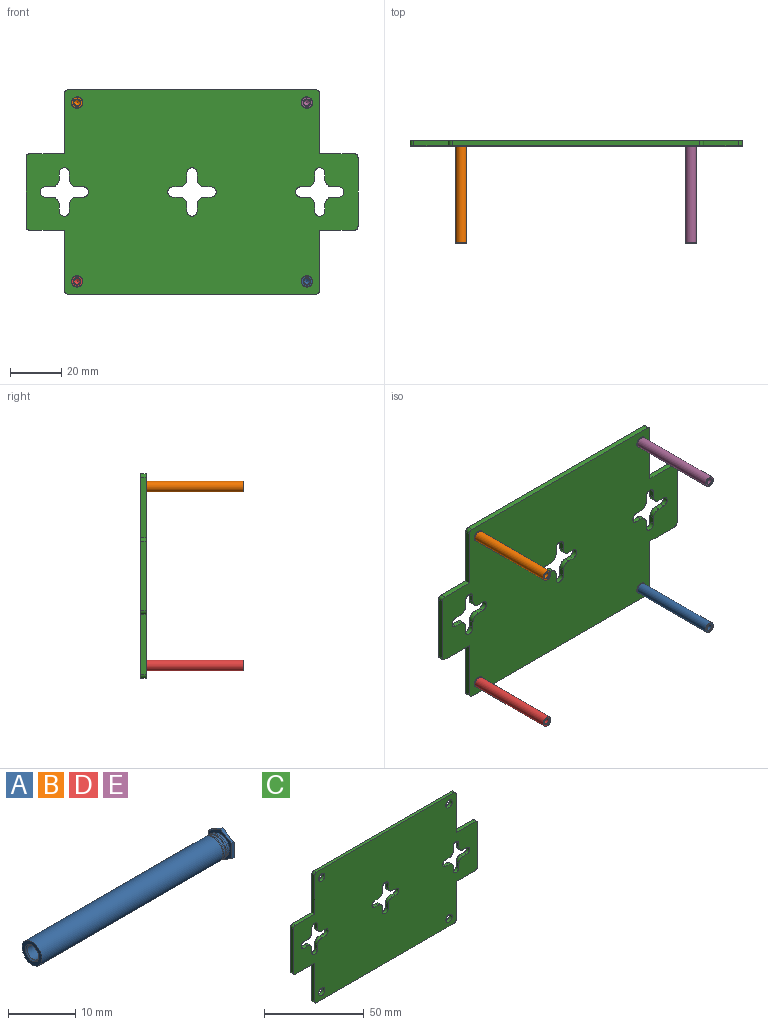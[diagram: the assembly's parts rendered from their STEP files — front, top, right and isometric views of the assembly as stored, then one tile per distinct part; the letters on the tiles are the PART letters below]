
ASSEMBLY  parts=5 mates=1
PART A: 25 faces, bbox 40x4.8x5.5 mm
  f0: plane 5.54x4.8mm, normal (1,0,0), area 20mm2, adj f1,f2,f3,f4,f5,f6
  f1: plane 2.4x1.39mm, normal (0,-0.5,0.87), area 1.3mm2, adj f0,f2,f6,f7
  f2: plane 2.77x0.48mm, normal (0,-1,0), area 1.3mm2, adj f0,f1,f3,f7
  f3: plane 2.4x1.39mm, normal (0,-0.5,-0.87), area 1.3mm2, adj f0,f2,f4,f7
  f4: plane 2.4x1.39mm, normal (0,0.5,-0.87), area 1.3mm2, adj f0,f3,f5,f7
  f5: plane 2.77x0.48mm, normal (0,1,0), area 1.3mm2, adj f0,f4,f6,f7
  f6: plane 2.4x1.39mm, normal (0,0.5,0.87), area 1.3mm2, adj f0,f1,f5,f7
  f7: plane 5.54x4.8mm, normal (-1,0,0), area 8.7mm2, adj f1,f2,f3,f4,f5,f6,f8
  f8: cylinder r=1.89mm len=3.78mm, axis (1,0,0), area 5.7mm2, adj f7,f9
  f9: plane 4.2x4.2mm, normal (1,0,0), area 2.6mm2, adj f8,f10
  f10: cylinder r=2.1mm len=4.2mm, axis (1,0,0), area 4.4mm2, adj f9,f11
  f11: plane 4.2x4.2mm, normal (-1,0,0), area 1.4mm2, adj f10,f12
  f12: cylinder r=1.99mm len=3.99mm, axis (1,0,0), area 2.6mm2, adj f11,f14
  f13: cone r=0.61mm half-angle=60deg, axis (-1,0,0), area 5.5mm2, adj f15
  f14: plane 4.2x4.2mm, normal (1,0,0), area 1.4mm2, adj f12,f16
  f15: cylinder r=1.23mm len=7.75mm, axis (-1,0,0), area 59.9mm2, adj f13,f17
  f16: cylinder r=2.1mm len=4.2mm, axis (1,0,0), area 4.4mm2, adj f14,f18
  f17: plane 2.46x2.46mm, normal (1,0,0), area 0mm2, adj f15,f19
  f18: plane 4.2x4.2mm, normal (-1,0,0), area 1.4mm2, adj f16,f20
  f19: cylinder r=1.22mm len=24.3mm, axis (-1,0,0), area 187mm2, adj f17,f24
  f20: cylinder r=1.99mm len=3.99mm, axis (1,0,0), area 2.6mm2, adj f18,f21
  f21: plane 4.2x4.2mm, normal (1,0,0), area 1.4mm2, adj f20,f23
  f22: plane 4.2x4.2mm, normal (-1,0,0), area 7.5mm2, adj f23,f24
  f23: cylinder r=2.1mm len=37.95mm, axis (1,0,0), area 500.7mm2, adj f21,f22
  f24: cone r=1.22mm half-angle=45deg, axis (-1,0,0), area 2.4mm2, adj f19,f22
PART B: same geometry as A
PART C: 74 faces, bbox 130x2x80 mm
  f0: plane 23.5x2mm, normal (-1,0,0), area 47mm2, adj f6,f7,f11,f73
  f1: plane 23.5x2mm, normal (1,0,0), area 47mm2, adj f6,f7,f10,f70
  f2: plane 23.5x2mm, normal (-1,0,0), area 47mm2, adj f6,f7,f12,f71
  f3: plane 97x2mm, normal (0,0,-1), area 194mm2, adj f6,f7,f71,f72
  f4: plane 23.5x2mm, normal (1,0,0), area 47mm2, adj f6,f7,f9,f72
  f5: plane 97x2mm, normal (0,0,1), area 194mm2, adj f6,f7,f70,f73
  f6: plane 130x80mm, normal (0,-1,0), area 8421.9mm2, adj f0,f1,f2,f3,f4,f5,f8,f9
  f7: plane 130x80mm, normal (0,1,0), area 8421.9mm2, adj f0,f1,f2,f3,f4,f5,f8,f9
  f8: plane 27x2mm, normal (1,0,0), area 54mm2, adj f6,f7,f68,f69
  f9: plane 13.5x2mm, normal (0,0,-1), area 27mm2, adj f4,f6,f7,f68
  f10: plane 13.5x2mm, normal (0,0,1), area 27mm2, adj f1,f6,f7,f69
  f11: plane 13.5x2mm, normal (0,0,1), area 27mm2, adj f0,f6,f7,f66
  f12: plane 13.5x2mm, normal (0,0,-1), area 27mm2, adj f2,f6,f7,f67
  f13: plane 27x2mm, normal (-1,0,0), area 54mm2, adj f6,f7,f66,f67
  f14: cylinder r=2.25mm len=4.5mm, axis (0,-1,0), area 28.3mm2, adj f6,f7
  f15: plane 2.5x2mm, normal (1,0,0), area 5mm2, adj f6,f7,f26,f56
  f16: plane 2.5x2mm, normal (0,0,-1), area 5mm2, adj f6,f7,f17,f56
  f17: cylinder r=2mm len=4mm, axis (0,-1,0), area 12.6mm2, adj f6,f7,f16,f18
  f18: plane 2.5x2mm, normal (0,0,1), area 5mm2, adj f6,f7,f17,f55
  f19: plane 2.5x2mm, normal (1,0,0), area 5mm2, adj f6,f7,f20,f55
  f20: cylinder r=2mm len=4mm, axis (0,-1,0), area 12.6mm2, adj f6,f7,f19,f21
  f21: plane 2.5x2mm, normal (-1,0,0), area 5mm2, adj f6,f7,f20,f54
  f22: plane 2.5x2mm, normal (0,0,1), area 5mm2, adj f6,f7,f23,f54
  f23: cylinder r=2mm len=4mm, axis (0,-1,0), area 12.6mm2, adj f6,f7,f22,f24
  f24: plane 2.5x2mm, normal (0,0,-1), area 5mm2, adj f6,f7,f23,f57
  f25: plane 2.5x2mm, normal (-1,0,0), area 5mm2, adj f6,f7,f26,f57
  f26: cylinder r=2mm len=4mm, axis (0,-1,0), area 12.6mm2, adj f6,f7,f15,f25
  f27: plane 2.5x2mm, normal (1,0,0), area 5mm2, adj f6,f7,f38,f60
  f28: plane 2.5x2mm, normal (0,0,-1), area 5mm2, adj f6,f7,f29,f60
  f29: cylinder r=2mm len=4mm, axis (0,-1,0), area 12.6mm2, adj f6,f7,f28,f30
  f30: plane 2.5x2mm, normal (0,0,1), area 5mm2, adj f6,f7,f29,f59
  f31: plane 2.5x2mm, normal (1,0,0), area 5mm2, adj f6,f7,f32,f59
  f32: cylinder r=2mm len=4mm, axis (0,-1,0), area 12.6mm2, adj f6,f7,f31,f33
  f33: plane 2.5x2mm, normal (-1,0,0), area 5mm2, adj f6,f7,f32,f58
  f34: plane 2.5x2mm, normal (0,0,1), area 5mm2, adj f6,f7,f35,f58
  f35: cylinder r=2mm len=4mm, axis (0,-1,0), area 12.6mm2, adj f6,f7,f34,f36
  f36: plane 2.5x2mm, normal (0,0,-1), area 5mm2, adj f6,f7,f35,f61
  f37: plane 2.5x2mm, normal (-1,0,0), area 5mm2, adj f6,f7,f38,f61
  f38: cylinder r=2mm len=4mm, axis (0,-1,0), area 12.6mm2, adj f6,f7,f27,f37
  f39: cylinder r=2.25mm len=4.5mm, axis (0,-1,0), area 28.3mm2, adj f6,f7
  f40: cylinder r=2.25mm len=4.5mm, axis (0,-1,0), area 28.3mm2, adj f6,f7
  f41: cylinder r=2.25mm len=4.5mm, axis (0,-1,0), area 28.3mm2, adj f6,f7
  f42: plane 2.5x2mm, normal (1,0,0), area 5mm2, adj f6,f7,f53,f64
  f43: plane 2.5x2mm, normal (0,0,-1), area 5mm2, adj f6,f7,f44,f64
  f44: cylinder r=2mm len=4mm, axis (0,-1,0), area 12.6mm2, adj f6,f7,f43,f45
  f45: plane 2.5x2mm, normal (0,0,1), area 5mm2, adj f6,f7,f44,f62
  f46: plane 2.5x2mm, normal (1,0,0), area 5mm2, adj f6,f7,f47,f62
  f47: cylinder r=2mm len=4mm, axis (0,-1,0), area 12.6mm2, adj f6,f7,f46,f48
  f48: plane 2.5x2mm, normal (-1,0,0), area 5mm2, adj f6,f7,f47,f63
  f49: plane 2.5x2mm, normal (0,0,1), area 5mm2, adj f6,f7,f50,f63
  f50: cylinder r=2mm len=4mm, axis (0,-1,0), area 12.6mm2, adj f6,f7,f49,f51
  f51: plane 2.5x2mm, normal (0,0,-1), area 5mm2, adj f6,f7,f50,f65
  f52: plane 2.5x2mm, normal (-1,0,0), area 5mm2, adj f6,f7,f53,f65
  f53: cylinder r=2mm len=4mm, axis (0,-1,0), area 12.6mm2, adj f6,f7,f42,f52
  f54: cylinder r=3mm len=3mm, axis (0,1,0), area 9.4mm2, adj f6,f7,f21,f22
  f55: cylinder r=3mm len=3mm, axis (0,-1,0), area 9.4mm2, adj f6,f7,f18,f19
  f56: cylinder r=3mm len=3mm, axis (0,1,0), area 9.4mm2, adj f6,f7,f15,f16
  f57: cylinder r=3mm len=3mm, axis (0,-1,0), area 9.4mm2, adj f6,f7,f24,f25
  f58: cylinder r=3mm len=3mm, axis (0,1,0), area 9.4mm2, adj f6,f7,f33,f34
  f59: cylinder r=3mm len=3mm, axis (0,-1,0), area 9.4mm2, adj f6,f7,f30,f31
  f60: cylinder r=3mm len=3mm, axis (0,1,0), area 9.4mm2, adj f6,f7,f27,f28
  f61: cylinder r=3mm len=3mm, axis (0,-1,0), area 9.4mm2, adj f6,f7,f36,f37
  f62: cylinder r=3mm len=3mm, axis (0,-1,0), area 9.4mm2, adj f6,f7,f45,f46
  f63: cylinder r=3mm len=3mm, axis (0,1,0), area 9.4mm2, adj f6,f7,f48,f49
  f64: cylinder r=3mm len=3mm, axis (0,1,0), area 9.4mm2, adj f6,f7,f42,f43
  f65: cylinder r=3mm len=3mm, axis (0,-1,0), area 9.4mm2, adj f6,f7,f51,f52
  f66: cylinder r=1.5mm len=2mm, axis (0,1,0), area 4.7mm2, adj f6,f7,f11,f13
  f67: cylinder r=1.5mm len=2mm, axis (0,-1,0), area 4.7mm2, adj f6,f7,f12,f13
  f68: cylinder r=1.5mm len=2mm, axis (0,1,0), area 4.7mm2, adj f6,f7,f8,f9
  f69: cylinder r=1.5mm len=2mm, axis (0,-1,0), area 4.7mm2, adj f6,f7,f8,f10
  f70: cylinder r=1.5mm len=2mm, axis (0,-1,0), area 4.7mm2, adj f1,f5,f6,f7
  f71: cylinder r=1.5mm len=2mm, axis (0,-1,0), area 4.7mm2, adj f2,f3,f6,f7
  f72: cylinder r=1.5mm len=2mm, axis (0,1,0), area 4.7mm2, adj f3,f4,f6,f7
  f73: cylinder r=1.5mm len=2mm, axis (0,1,0), area 4.7mm2, adj f0,f5,f6,f7
PART D: same geometry as A
PART E: same geometry as A
PLACE A rot(axis=(0,0,1),90deg) t=(45,-0.48,-35)mm
PLACE B rot(axis=(0,0,1),90deg) t=(-45,-0.48,35)mm
PLACE C at identity
PLACE D rot(axis=(0,0,1),90deg) t=(-45,-0.48,-35)mm
PLACE E rot(axis=(0,0,1),90deg) t=(45,-0.48,35)mm
MATE fastened D.f13 <-> C.f40  axis (0,1,0) through (-45,0,-35)mm
